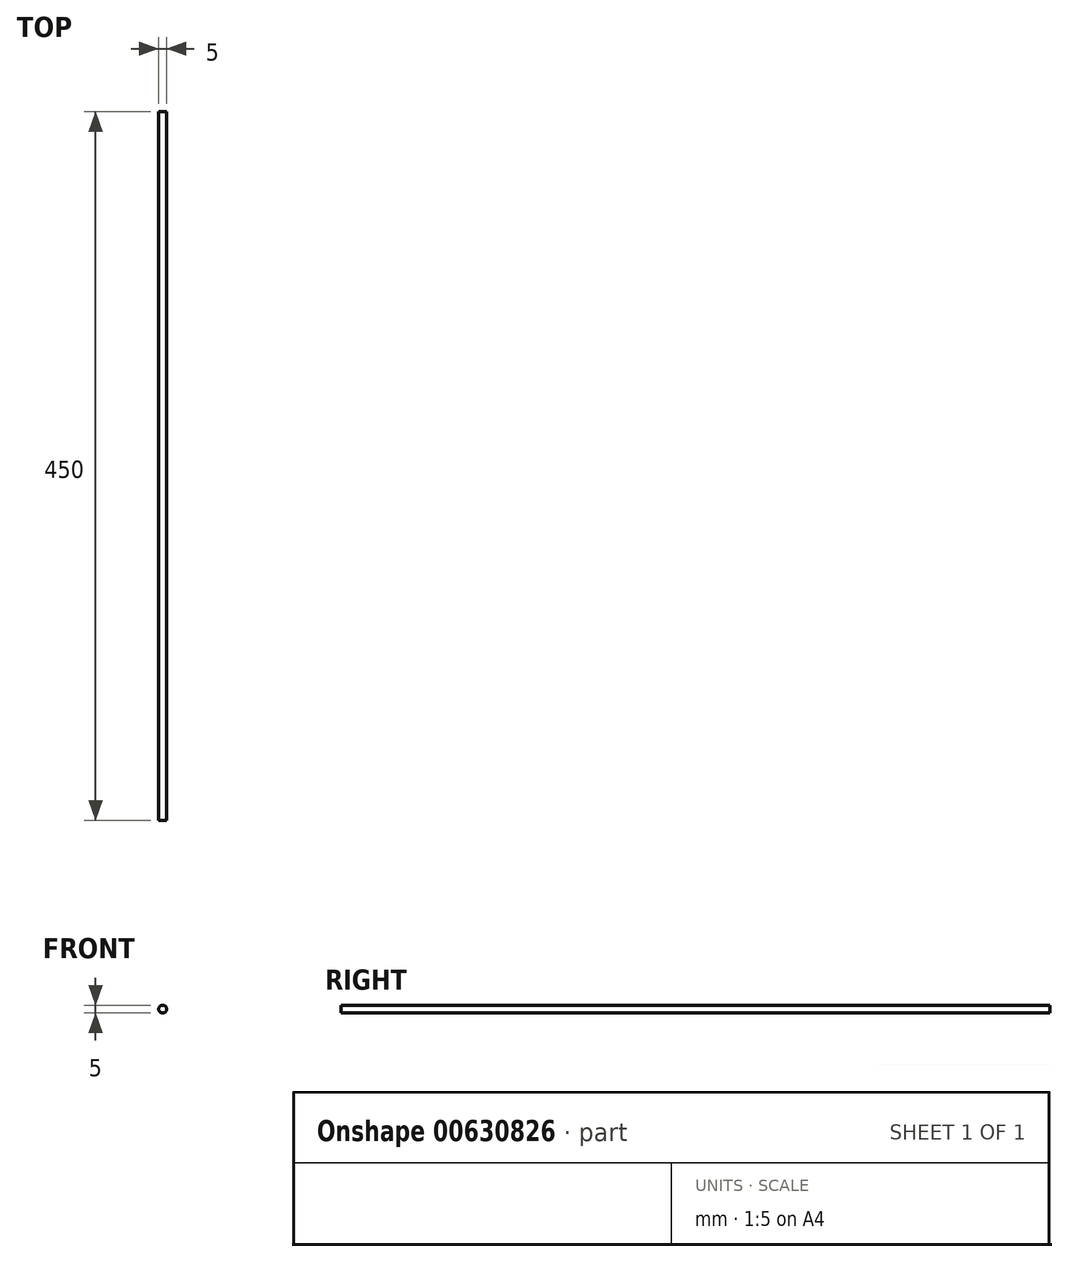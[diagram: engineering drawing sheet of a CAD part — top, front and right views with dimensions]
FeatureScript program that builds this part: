
annotation { "Feature Type Name" : "Feature", "Feature Type Description" : "" }
export const myFeature = defineFeature(function(context is Context, id is Id, definition is map)
    precondition{}
    {
        {
            var Q0;
            Q0=qCreatedBy(makeId("Front.planeOp"),FACE);
            var sketch = newSketch(context, id + "F0", { "sketchPlane" : qUnion([Q0])});
            skCircle(sketch, "E0", {"center": v(0, 0) * mm, "radius": 2.5 * mm});
            skSolve(sketch);
        }
        {
            var Q0;
            Q0=makeQuery(id+"F0.imprint","IMPRINT",FACE,{"disambiguationData":[TD([[makeQuery(id+"F0.imprint","IMPRINT",EDGE,{"derivedFrom":sQuery(id+"F0.wireOp",EDGE,"E0")}),1.0]])]});
            extrude(context, id + "F1", {"entities" : qUnion([Q0]), "depth" : 450 * mm, "offsetDistance" : 25 * mm});
        }
    });
